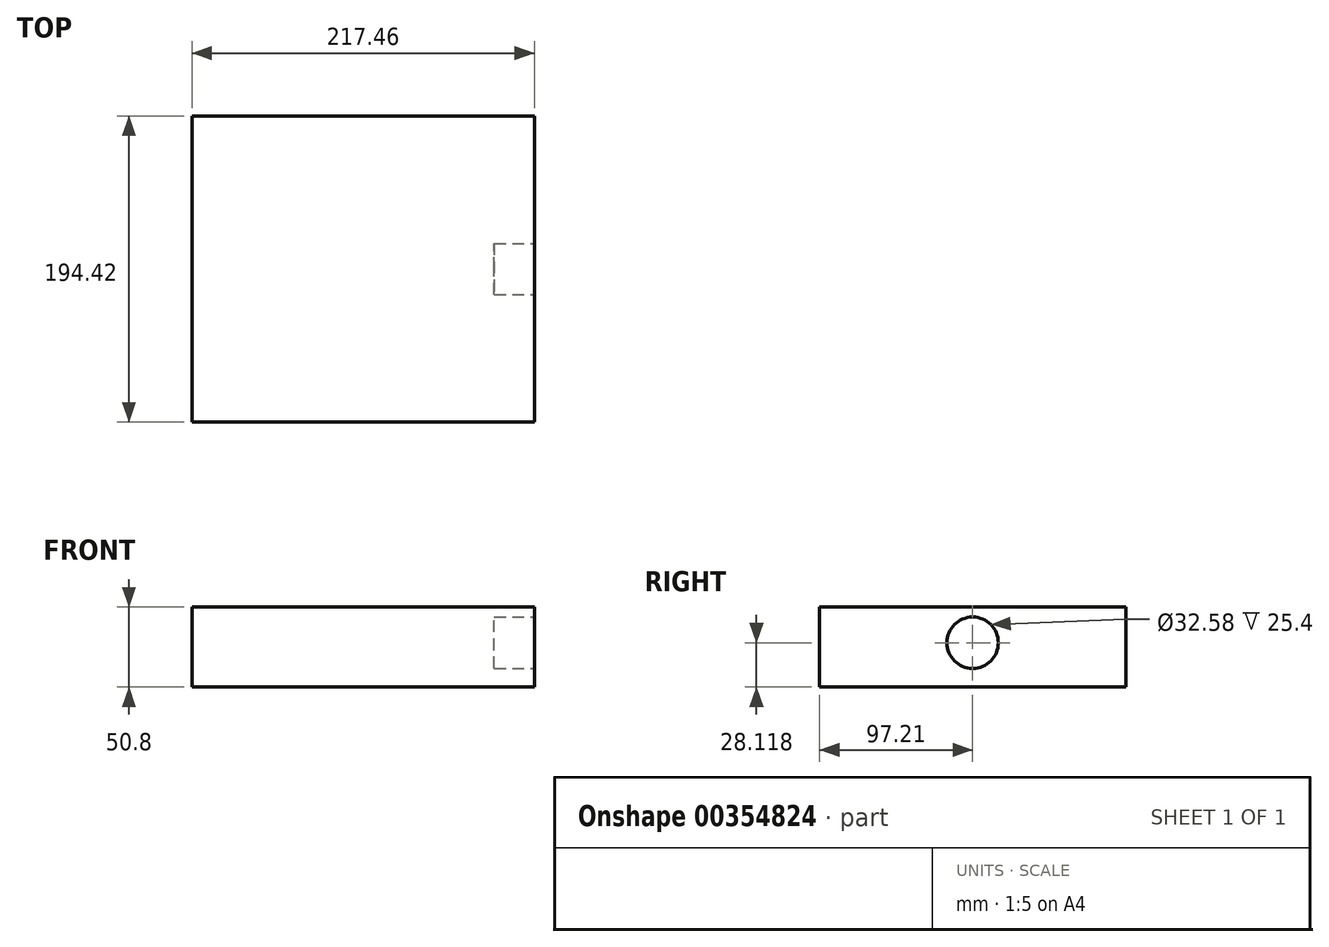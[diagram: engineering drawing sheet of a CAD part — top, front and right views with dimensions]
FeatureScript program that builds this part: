
annotation { "Feature Type Name" : "Feature", "Feature Type Description" : "" }
export const myFeature = defineFeature(function(context is Context, id is Id, definition is map)
    precondition{}
    {
        {
            var Q0;
            Q0=qCreatedBy(makeId("Top.planeOp"),FACE);
            var sketch = newSketch(context, id + "F0", { "sketchPlane" : qUnion([Q0])});
            skLineSegment(sketch, "E0.bottom", {"start": v(108.73, -97.21) * mm, "end": v(-108.73, -97.21) * mm});
            skLineSegment(sketch, "E0.top", {"start": v(108.73, 97.21) * mm, "end": v(-108.73, 97.21) * mm});
            skLineSegment(sketch, "E0.left", {"start": v(108.73, -97.21) * mm, "end": v(108.73, 97.21) * mm});
            skLineSegment(sketch, "E0.right", {"start": v(-108.73, -97.21) * mm, "end": v(-108.73, 97.21) * mm});
            skPoint(sketch, "E0.middle", {"position": v(0, 0) * mm});
            skSolve(sketch);
        }
        {
            var Q0;
            Q0=makeQuery(id+"F0.imprint","IMPRINT",FACE,{"disambiguationData":[TD([[makeQuery(id+"F0.imprint","IMPRINT",EDGE,{"derivedFrom":sQuery(id+"F0.wireOp",EDGE,"E0.bottom")}),-1.0]])]});
            extrude(context, id + "F1", {"entities" : qUnion([Q0]), "depth" : 50.8 * mm});
        }
        {
            var Q0;
            Q0=makeQuery(id+"F1.opExtrude","SWEPT_FACE",FACE,{"disambiguationData":[OSD([sQuery(id+"F0.wireOp",EDGE,"E0.left")])]});
            var sketch = newSketch(context, id + "F2", { "sketchPlane" : qUnion([Q0])});
            skCircle(sketch, "E1", {"center": v(0, 28.12) * mm, "radius": 16.29 * mm});
            skSolve(sketch);
        }
        {
            var Q0;
            Q0 = qSketchRegion(id + "F2", true);
            extrude(context, id + "F3", {"entities" : qUnion([Q0]), "operationType" : NewBodyOperationType.REMOVE, "oppositeDirection" : true, "depth" : 25.4 * mm});
        }
    });
